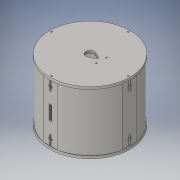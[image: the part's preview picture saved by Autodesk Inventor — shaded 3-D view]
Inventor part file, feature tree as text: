
AUTODESK INVENTOR PART (.ipt)
format: ipt  version: 2016 (Build 200138000, 138)  size: 353,792 bytes
history: native  units: in
note: dims shown in document units (in); Inventor stores cm internally (conversion verified against a paired STEP export)
features: extrude x8, sketch x8
ambient origin geometry x8: Origin, YZ Plane, XZ Plane, XY Plane, X Axis, Y Axis, Z Axis, Center Point
bodies: Solid1 (feature_tree)
feature tree (16):
  extrude  "Extrusion1"  Depth=0.053in
  sketch  "Sketch2"  dims[d1=0.5in d2=0.75in d3=0.135in d4=0.15in d5=0.053in d6=0.2925in d7=0.2925in d8=0.053in d9=0.053in d10=0.6in d11=0.2in d13=0.803in d14=0.3545in]
  extrude  "Extrusion7"  Depth=0.3605in
  extrude  "Extrusion8"  Depth=0.18in TaperAngle=0.0deg
  extrude  "Extrusion9"  Depth=5.5in
  extrude  "Extrusion10"  Depth=0.23in
  extrude  "Extrusion11"  Depth=0.23in
  extrude  "Extrusion12"  Depth=0.0625in
  extrude  "Extrusion13"  Depth=0.0625in
  sketch  "Sketch1"  dims[d0=5.59in]
  sketch  "Sketch4"  dims[d15=0.3075in d16=0.3605in]
  sketch  "Sketch6"  dims[d17=0.0248in d18=0.18in d19=0.0in]
  sketch  "Sketch7"  dims[d20=5.5in d21=5.14in]
  sketch  "Sketch8"  dims[d29=0.105in d30=0.23in]
  sketch  "Sketch9"  dims[d31=0.105in d32=0.23in]
  sketch  "Sketch10"  dims[d33=0.0625in d34=0.0625in d35=0.0625in d36=0.2292in d37=0.105in d38=0.7in d41=2.455in d42=1.3in d47=0.5in d49=0.5in d53=0.5in d58=0.5in d60=0.5in d62=1.0in d63=45.0deg d64=1.0in d65=135.0deg d66=1.0in d67=90.0deg d68=1.0in d69=90.0deg d70=3.0266in d71=3.0266in d72=3.0266in d73=3.0266in d74=0.1956in d75=1.0in d76=2.9456in d77=1.0in d78=2.9456in d79=1.0in d80=2.9456in d81=2.9456in d82=1.0in d83=2.9456in d84=2.9456in d85=4.0in d86=0.0in d87=10.0in d88=0.0in d89=0.18in d90=0.0in d91=5.5902in d92=2.495in d106=0.063in d107=0.105in d108=0.063in d109=0.366in d110=0.366in d111=0.063in d112=0.105in d113=0.229in d114=0.105in d119=10.0in d120=0.0in d121=0.2in d122=0.0in d123=0.2in d124=0.0in d125=0.19in d126=1.0in d127=0.2in d128=0.0in]
